AUTODESK INVENTOR PART (.ipt)
format: ipt  version: 2021 (Build 250183000, 183)  size: 144,384 bytes
history: native  units: mm
features: fillet x6, extrude x2, sketch x2
ambient origin geometry x8: Origin, YZ Plane, XZ Plane, XY Plane, X Axis, Y Axis, Z Axis, Center Point
bodies: Solid1 (feature_tree)
feature tree (10):
  extrude  "Extrusion1"  Depth=12.6mm
  fillet  "Fillet1"  Radius=2.0mm
  fillet  "Fillet2"  Radius=1.0mm
  fillet  "Fillet3"  Radius=1.0mm
  extrude  "Extrusion2"  Depth=4.0mm TaperAngle=0.0deg
  fillet  "Fillet4"  Radius=2.0mm
  fillet  "Fillet5"  Radius=2.0mm
  fillet  "Fillet6"  Radius=1.0mm
  sketch  "Sketch1"  dims[d0=8.2mm d1=12.6mm d2=2.0mm d3=1.0mm d4=1.0mm]
  sketch  "Sketch2"  dims[d5=2.0mm d6=4.0mm d7=0.0mm d8=2.0mm d9=2.0mm d10=1.0mm d11=2.0mm d12=2.0mm d13=0.0mm d14=0.0mm d15=0.5mm d16=1.0mm d17=0.3mm]
